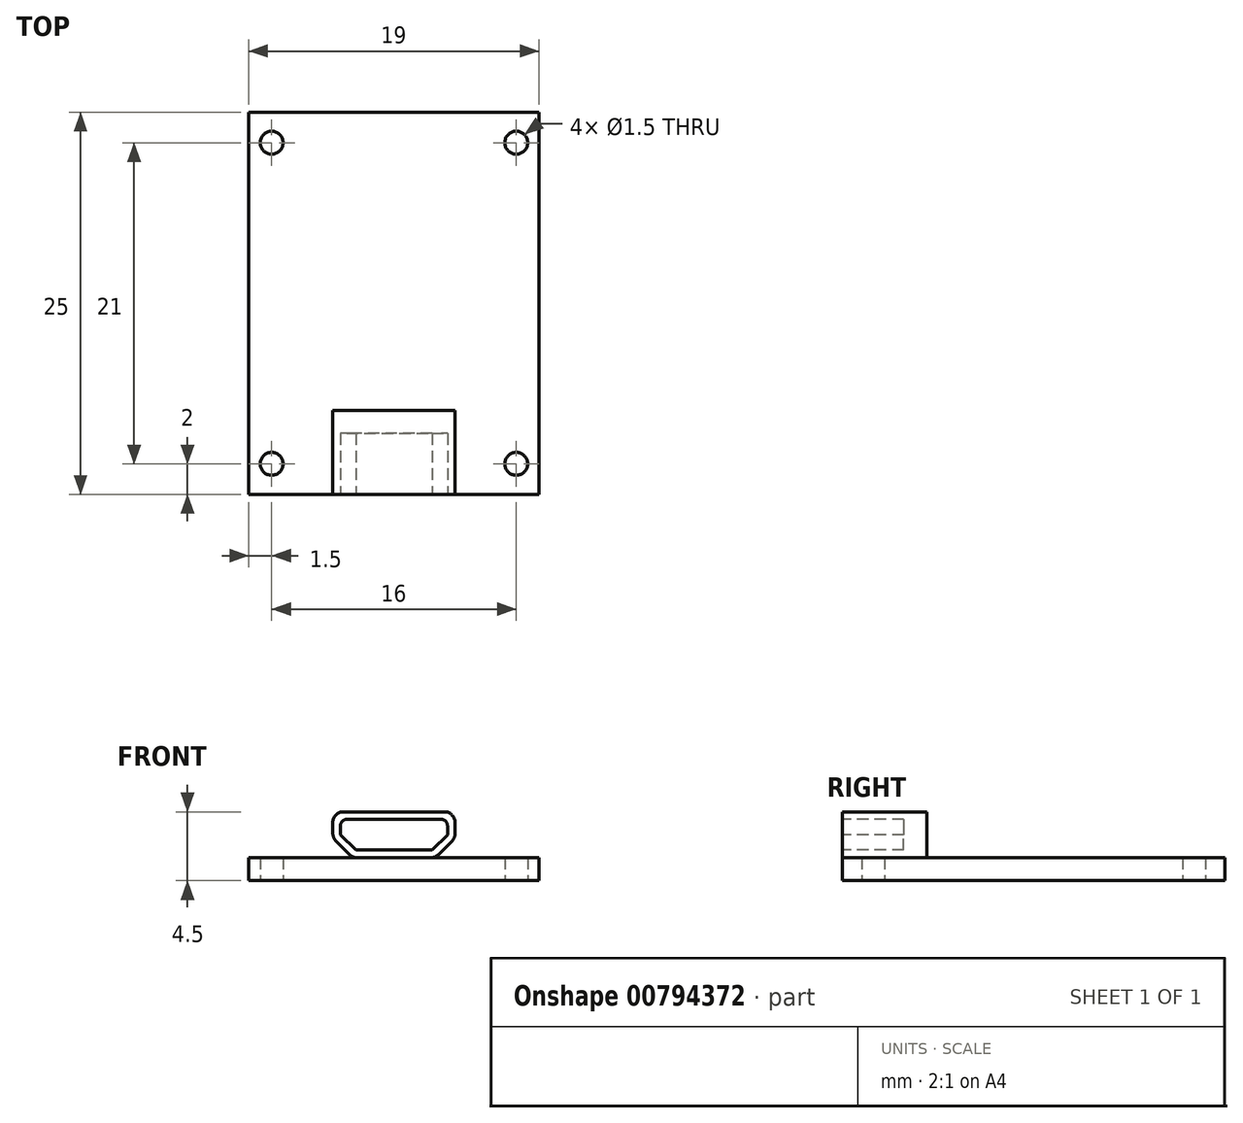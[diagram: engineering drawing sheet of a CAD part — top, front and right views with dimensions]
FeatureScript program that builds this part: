
annotation { "Feature Type Name" : "Feature", "Feature Type Description" : "" }
export const myFeature = defineFeature(function(context is Context, id is Id, definition is map)
    precondition{}
    {
        {
            var Q0;
            Q0=qCreatedBy(makeId("Top.planeOp"),FACE);
            var sketch = newSketch(context, id + "F0", { "sketchPlane" : qUnion([Q0])});
            skLineSegment(sketch, "E0.bottom", {"start": v(9.5, -12.5) * mm, "end": v(-9.5, -12.5) * mm});
            skLineSegment(sketch, "E0.top", {"start": v(9.5, 12.5) * mm, "end": v(-9.5, 12.5) * mm});
            skLineSegment(sketch, "E0.left", {"start": v(9.5, -12.5) * mm, "end": v(9.5, 12.5) * mm});
            skLineSegment(sketch, "E0.right", {"start": v(-9.5, -12.5) * mm, "end": v(-9.5, 12.5) * mm});
            skPoint(sketch, "E0.middle", {"position": v(0, 0) * mm});
            skLineSegment(sketch, "E1", {"start": v(13.1, 0) * mm, "end": v(-13.63, 0) * mm, "construction": true});
            skLineSegment(sketch, "E2", {"start": v(0, 14.59) * mm, "end": v(0, -15.52) * mm, "construction": true});
            skCircle(sketch, "E3", {"center": v(-8, 10.5) * mm, "radius": 0.75 * mm});
            skCircle(sketch, "E4.MirrorC", {"center": v(8, 10.5) * mm, "radius": 0.75 * mm});
            skCircle(sketch, "E5.MirrorC", {"center": v(-8, -10.5) * mm, "radius": 0.75 * mm});
            skCircle(sketch, "E6.MirrorC", {"center": v(8, -10.5) * mm, "radius": 0.75 * mm});
            skSolve(sketch);
        }
        {
            var Q0;
            Q0 = qSketchRegion(id + "F0", true);
            extrude(context, id + "F1", {"entities" : qUnion([Q0]), "depth" : 1.5 * mm, "offsetDistance" : 25 * mm});
        }
        {
            var Q0;
            Q0=makeQuery(id+"F1.opExtrude","SWEPT_FACE",FACE,{"disambiguationData":[OSD([sQuery(id+"F0.wireOp",EDGE,"E0.bottom")])]});
            var sketch = newSketch(context, id + "F2", { "sketchPlane" : qUnion([Q0])});
            skLineSegment(sketch, "E7", {"start": v(0, -1.8) * mm, "end": v(0, 8.4) * mm, "construction": true});
            skLineSegment(sketch, "E8", {"start": v(0, 1.5) * mm, "end": v(2.41, 1.5) * mm});
            skLineSegment(sketch, "E9", {"start": v(0, 4.5) * mm, "end": v(3.3, 4.5) * mm});
            skLineSegment(sketch, "E10", {"start": v(4, 3.8) * mm, "end": v(4, 3.09) * mm});
            skLineSegment(sketch, "E11", {"start": v(2.9, 1.7) * mm, "end": v(3.8, 2.6) * mm});
            skPoint(sketch, "E12.visualSharp", {"position": v(4, 4.5) * mm});
            skArc(sketch, "E12.filletArc", {"start": v(4, 3.8) * mm, "mid": v(3.8, 4.3) * mm, "end": v(3.3, 4.5) * mm});
            skPoint(sketch, "E13.visualSharp", {"position": v(4, 2.8) * mm});
            skArc(sketch, "E13.filletArc", {"start": v(3.8, 2.6) * mm, "mid": v(3.95, 2.82) * mm, "end": v(4, 3.09) * mm});
            skPoint(sketch, "E14.visualSharp", {"position": v(2.7, 1.5) * mm});
            skArc(sketch, "E14.filletArc", {"start": v(2.41, 1.5) * mm, "mid": v(2.68, 1.55) * mm, "end": v(2.9, 1.7) * mm});
            skArc(sketch, "E15.MirrorCS", {"start": v(-3.8, 2.6) * mm, "mid": v(-3.95, 2.82) * mm, "end": v(-4, 3.09) * mm});
            skArc(sketch, "E16.MirrorCS", {"start": v(-2.41, 1.5) * mm, "mid": v(-2.68, 1.55) * mm, "end": v(-2.9, 1.7) * mm});
            skArc(sketch, "E17.MirrorCS", {"start": v(-4, 3.8) * mm, "mid": v(-3.8, 4.3) * mm, "end": v(-3.3, 4.5) * mm});
            skLineSegment(sketch, "E18.MirrorCS", {"start": v(-2.9, 1.7) * mm, "end": v(-3.8, 2.6) * mm});
            skLineSegment(sketch, "E19.MirrorCS", {"start": v(-4, 3.8) * mm, "end": v(-4, 3.09) * mm});
            skLineSegment(sketch, "E20.MirrorCS", {"start": v(0, 4.5) * mm, "end": v(-3.3, 4.5) * mm});
            skLineSegment(sketch, "E21.MirrorCS", {"start": v(0, 1.5) * mm, "end": v(-2.41, 1.5) * mm});
            skPoint(sketch, "E22.MirrorP", {"position": v(-4, 4.5) * mm});
            skPoint(sketch, "E23.MirrorP", {"position": v(-4, 2.8) * mm});
            skPoint(sketch, "E24.MirrorP", {"position": v(-2.7, 1.5) * mm});
            skLineSegment(sketch, "E25.0", {"start": v(0, 4) * mm, "end": v(3.1, 4) * mm});
            skLineSegment(sketch, "E25.1", {"start": v(3.5, 3.6) * mm, "end": v(3.5, 3) * mm});
            skLineSegment(sketch, "E25.2", {"start": v(0, 4) * mm, "end": v(-3.1, 4) * mm});
            skLineSegment(sketch, "E25.3", {"start": v(2.5, 2) * mm, "end": v(3.5, 3) * mm});
            skLineSegment(sketch, "E25.4", {"start": v(-3.5, 3.6) * mm, "end": v(-3.5, 3) * mm});
            skLineSegment(sketch, "E25.5", {"start": v(-2.5, 2) * mm, "end": v(-3.5, 3) * mm});
            skLineSegment(sketch, "E25.6", {"start": v(0, 2) * mm, "end": v(-2.5, 2) * mm});
            skLineSegment(sketch, "E25.7", {"start": v(0, 2) * mm, "end": v(2.5, 2) * mm});
            skPoint(sketch, "E26.visualSharp", {"position": v(-3.5, 4) * mm});
            skArc(sketch, "E26.filletArc", {"start": v(-3.1, 4) * mm, "mid": v(-3.38, 3.88) * mm, "end": v(-3.5, 3.6) * mm});
            skPoint(sketch, "E27.visualSharp", {"position": v(3.5, 4) * mm});
            skArc(sketch, "E27.filletArc", {"start": v(3.5, 3.6) * mm, "mid": v(3.38, 3.88) * mm, "end": v(3.1, 4) * mm});
            skSolve(sketch);
        }
        {
            var Q0;
            Q0 = qSketchRegion(id + "F2", true);
            var Q1;
            Q1=makeQuery(id+"F2.imprint","IMPRINT",FACE,{"disambiguationData":[TD([[makeQuery(id+"F2.imprint","IMPRINT",EDGE,{"derivedFrom":sQuery(id+"F2.wireOp",EDGE,"E25.0")}),-1.0]])]});
            extrude(context, id + "F3", {"entities" : qUnion([Q0, Q1]), "oppositeDirection" : true, "depth" : 5.5 * mm, "offsetDistance" : 25 * mm});
        }
        {
            var Q0;
            Q0=makeQuery(id+"F2.imprint","IMPRINT",FACE,{"disambiguationData":[TD([[makeQuery(id+"F2.imprint","IMPRINT",EDGE,{"derivedFrom":sQuery(id+"F2.wireOp",EDGE,"E25.0")}),-1.0]])]});
            extrude(context, id + "F4", {"entities" : qUnion([Q0]), "operationType" : NewBodyOperationType.REMOVE, "oppositeDirection" : true, "depth" : 4 * mm, "offsetDistance" : 25 * mm});
        }
    });
